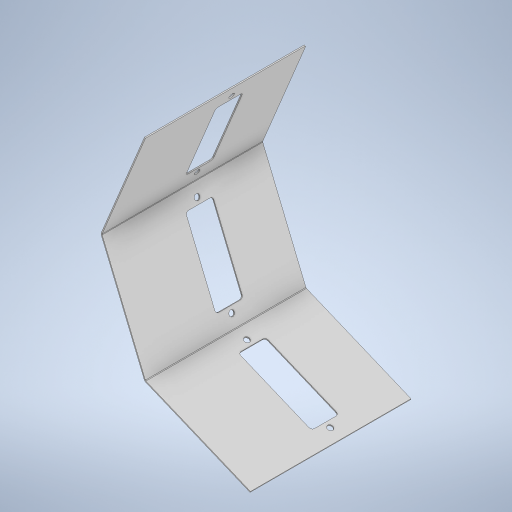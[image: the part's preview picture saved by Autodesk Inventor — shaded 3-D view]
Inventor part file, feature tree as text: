
AUTODESK INVENTOR PART (.ipt)
format: ipt  version: 2024.2 (Build 282272000, 272)  size: 508,928 bytes
history: native  units: mm
features: sheet_metal_op x3, sketch x3, extrude x2, other x2, fillet x1, pattern_circular x1, pattern_linear x1, chamfer x1, projected_geometry x1
ambient origin geometry x8: Origin, YZ Plane, XZ Plane, XY Plane, X Axis, Y Axis, Z Axis, Center Point
bodies: Body1 (feature_tree)
feature tree (15):
  sheet_metal_op  "Contour Flange3"
  extrude  "Extrusion4"  Depth=4.0mm
  fillet  "Fillet1"  Radius=0.9mm
  pattern_circular  "Circular Pattern2"  [2 undecoded]
  pattern_linear  "Rectangular Pattern2"  Spacing1=2.0mm  [1 undecoded]
  chamfer  "Corner Round1"
  extrude  "Extrusion5"  Depth=2.0mm
  sketch  "Sketch2"  dims[d58=4.0mm d59=4.0mm d70=0.9mm]
  other  "Plate6"
  sheet_metal_op  "Bend6"
  sheet_metal_op  "Corner6"
  sketch  "Sketch11"  dims[d72=0.9mm]
  projected_geometry  "Projected Loop1"
  sketch  "Sketch12"  dims[d74=506.0mm d75=2.0mm d76=2.0mm d77=1.0mm d78=4.0mm d79=2.0mm d80=2006.0mm d81=2.0mm d82=3.0mm d83=8.0mm d84=2.0mm d85=2.0mm d141=50.0mm d142=145.0mm d143=10.0mm d145=125.0mm d146=10.0mm d147=10.0mm d148=0.0mm d149=5.0mm d150=30.0mm d151=90.0deg d153=80.0mm d155=250.0mm d156=2.0mm d157=600.0mm d158=1712.25mm d159=600.0mm d160=0.0mm]
  other  "Definition1"
note: 3 required parameter values undecoded (feature->parameter linkage not recoverable at this tier; creation-order binding heuristic only, values carry confidence <= 0.55)
